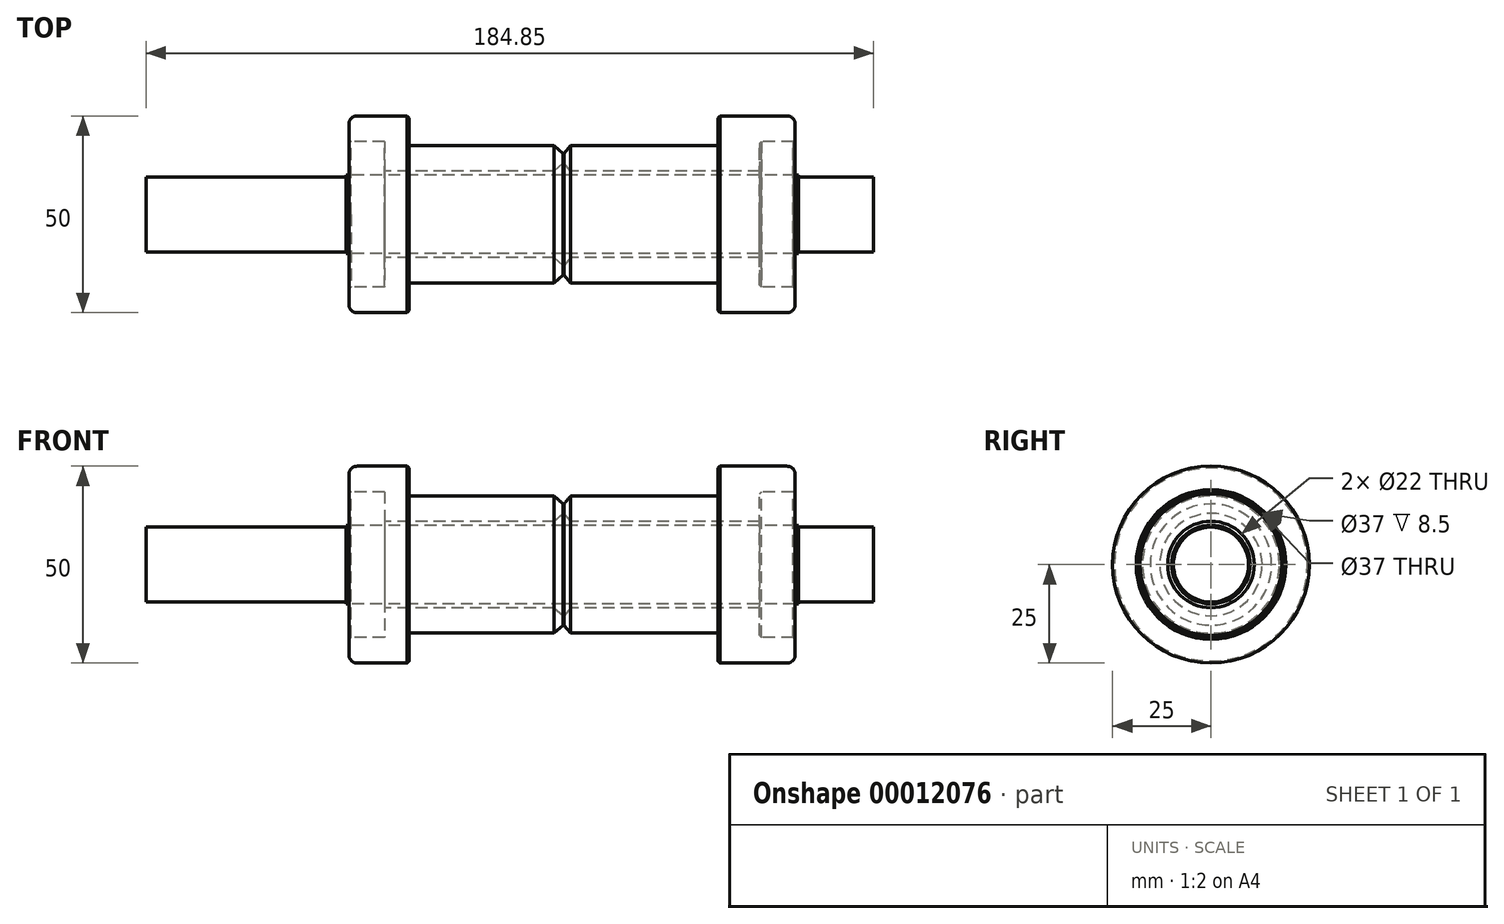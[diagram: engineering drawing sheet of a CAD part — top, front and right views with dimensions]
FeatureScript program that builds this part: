
annotation { "Feature Type Name" : "Feature", "Feature Type Description" : "" }
export const myFeature = defineFeature(function(context is Context, id is Id, definition is map)
    precondition{}
    {
        {
            var Q0;
            Q0=qCreatedBy(makeId("Front.planeOp"),FACE);
            var sketch = newSketch(context, id + "F0", { "sketchPlane" : qUnion([Q0])});
            skLineSegment(sketch, "E0", {"start": v(2, 25) * mm, "end": v(15.3, 25) * mm});
            skLineSegment(sketch, "E1", {"start": v(15.3, 25) * mm, "end": v(15.3, 17.4) * mm});
            skLineSegment(sketch, "E2", {"start": v(15.3, 17.4) * mm, "end": v(52.1, 17.4) * mm});
            skLineSegment(sketch, "E3", {"start": v(44.13, 11) * mm, "end": v(9, 11) * mm});
            skLineSegment(sketch, "E4", {"start": v(0, 23) * mm, "end": v(0, 18.5) * mm});
            skLineSegment(sketch, "E5.0", {"start": v(9, 18.5) * mm, "end": v(9, 11) * mm});
            skLineSegment(sketch, "E6", {"start": v(0, 18.5) * mm, "end": v(9, 18.5) * mm});
            skPoint(sketch, "E7.orphan", {"position": v(0, 11) * mm});
            skLineSegment(sketch, "E8", {"start": v(0, 0) * mm, "end": v(27.15, 0) * mm, "construction": true});
            skLineSegment(sketch, "E9", {"start": v(54.5, 56.17) * mm, "end": v(54.5, 17.4) * mm, "construction": true});
            skLineSegment(sketch, "E10.MirrorCS", {"start": v(113.3, 18.5) * mm, "end": v(104.3, 18.5) * mm});
            skLineSegment(sketch, "E11.MirrorCS", {"start": v(44.18, 11) * mm, "end": v(52.1, 11) * mm});
            skLineSegment(sketch, "E12.MirrorCS", {"start": v(111.3, 25) * mm, "end": v(93.7, 25) * mm});
            skLineSegment(sketch, "E13.MirrorCS", {"start": v(93.7, 25) * mm, "end": v(93.7, 17.4) * mm});
            skLineSegment(sketch, "E14.MirrorCS", {"start": v(93.7, 17.4) * mm, "end": v(61.18, 17.4) * mm});
            skPoint(sketch, "E15.MirrorP", {"position": v(109, 11) * mm});
            skPoint(sketch, "E16.orphan", {"position": v(109, 18.5) * mm});
            skLineSegment(sketch, "E17", {"start": v(104.3, 18.5) * mm, "end": v(104.3, 11) * mm});
            skPoint(sketch, "E18.MirrorCS.end.orphan", {"position": v(100, 11) * mm});
            skPoint(sketch, "E18.MirrorCS.start.orphan", {"position": v(100, 18.5) * mm});
            skLineSegment(sketch, "E19", {"start": v(-0.8, 10) * mm, "end": v(114.2, 10) * mm});
            skLineSegment(sketch, "E20", {"start": v(-51.6, 9.52) * mm, "end": v(-0.8, 9.52) * mm});
            skLineSegment(sketch, "E21", {"start": v(133.25, 9.53) * mm, "end": v(133.25, 0) * mm});
            skLineSegment(sketch, "E22", {"start": v(-51.6, 9.52) * mm, "end": v(-51.6, 0) * mm});
            skLineSegment(sketch, "E23", {"start": v(133.25, 0) * mm, "end": v(-51.6, 0) * mm});
            skPoint(sketch, "E23.startSnap0", {"position": v(133.25, 1.56) * mm});
            skLineSegment(sketch, "E24.trimOffspring", {"start": v(114.2, 9.53) * mm, "end": v(133.25, 9.53) * mm});
            skPoint(sketch, "E25.orphan", {"position": v(-51.6, 10) * mm});
            skLineSegment(sketch, "E26.trimOffspring", {"start": v(114.2, 10) * mm, "end": v(114.2, 9.53) * mm});
            skPoint(sketch, "E27.orphan", {"position": v(133.25, 10) * mm});
            skPoint(sketch, "E28.orphan", {"position": v(133.25, -6.87) * mm});
            skLineSegment(sketch, "E29", {"start": v(113.3, 23) * mm, "end": v(113.3, 18.5) * mm});
            skLineSegment(sketch, "E30", {"start": v(44.13, 11) * mm, "end": v(44.18, 11) * mm});
            skLineSegment(sketch, "E31.0", {"start": v(54.4, 15.4) * mm, "end": v(54.4, 13) * mm});
            skLineSegment(sketch, "E32.0", {"start": v(54.6, 15.4) * mm, "end": v(54.6, 13) * mm});
            skLineSegment(sketch, "E33.trimOffspring", {"start": v(54.5, 11) * mm, "end": v(54.5, -20.93) * mm, "construction": true});
            skLineSegment(sketch, "E34.trimOffspring", {"start": v(54.4, 0) * mm, "end": v(54.4, -20.93) * mm});
            skLineSegment(sketch, "E35", {"start": v(59.13, 17.4) * mm, "end": v(61.18, 17.4) * mm});
            skLineSegment(sketch, "E36.trimOffspring", {"start": v(56.3, 17.4) * mm, "end": v(59.13, 17.4) * mm});
            skPoint(sketch, "E37.visualSharp", {"position": v(54.6, 17.4) * mm});
            skPoint(sketch, "E38.visualSharp", {"position": v(54.4, 17.4) * mm});
            skLineSegment(sketch, "E39", {"start": v(54.6, 15.4) * mm, "end": v(56.3, 17.4) * mm});
            skLineSegment(sketch, "E40", {"start": v(52.1, 17.4) * mm, "end": v(54.4, 15.4) * mm});
            skLineSegment(sketch, "E41.trimOffspring", {"start": v(56.3, 11) * mm, "end": v(104.3, 11) * mm});
            skPoint(sketch, "E42.visualSharp", {"position": v(54.6, 11) * mm});
            skPoint(sketch, "E43.visualSharp", {"position": v(54.4, 11) * mm});
            skLineSegment(sketch, "E44", {"start": v(54.6, 13) * mm, "end": v(56.3, 11) * mm});
            skLineSegment(sketch, "E45", {"start": v(52.1, 11) * mm, "end": v(54.4, 13) * mm});
            skPoint(sketch, "E46.visualSharp", {"position": v(113.3, 25) * mm});
            skArc(sketch, "E46.filletArc", {"start": v(113.3, 23) * mm, "mid": v(112.71, 24.41) * mm, "end": v(111.3, 25) * mm});
            skPoint(sketch, "E47.visualSharp", {"position": v(0, 25) * mm});
            skArc(sketch, "E47.filletArc", {"start": v(2, 25) * mm, "mid": v(0.59, 24.41) * mm, "end": v(0, 23) * mm});
            skLineSegment(sketch, "E48", {"start": v(-0.8, 9.52) * mm, "end": v(-0.8, 10) * mm});
            skSolve(sketch);
        }
        {
            var Q0;
            Q0=makeQuery(id+"F0.imprint","IMPRINT",FACE,{"disambiguationData":[TD([[makeQuery(id+"F0.imprint","IMPRINT",EDGE,{"derivedFrom":sQuery(id+"F0.wireOp",EDGE,"E0")}),-1.0]])]});
            var Q1;
            Q1=makeQuery(id+"F0.imprint","IMPRINT",FACE,{"disambiguationData":[TD([[makeQuery(id+"F0.imprint","IMPRINT",EDGE,{"derivedFrom":sQuery(id+"F0.wireOp",EDGE,"E10.MirrorCS")}),-1.0]])]});
            var Q2;
            Q2=makeQuery(id+"F0.imprint","IMPRINT",FACE,{"disambiguationData":[TD([[makeQuery(id+"F0.imprint","IMPRINT",EDGE,{"derivedFrom":sQuery(id+"F0.wireOp",EDGE,"E19")}),-1.0]])]});
            var Q3;
            Q3=sQuery(id+"F0.wireOp",EDGE,"E8");
            var Q4;
            Q4=sQuery(id+"F0.wireOp",EDGE,"E8");
            revolve(context, id + "F1", {"entities" : qUnion([Q0, Q1, Q2]), "surfaceEntities" : qUnion([Q3]), "axis" : qUnion([Q4]), "revolveType" : RevolveType.FULL});
        }
        {
            var Q0;
            Q0=makeQuery(id+"F1.opRevolve","SWEPT_EDGE",EDGE,{"disambiguationData":[OSD([sQuery(id+"F0.wireOp",EDGE,"E0"),sQuery(id+"F0.wireOp",EDGE,"E1")])]});
            var Q1;
            Q1=makeQuery(id+"F1.opRevolve","SWEPT_EDGE",EDGE,{"disambiguationData":[OSD([sQuery(id+"F0.wireOp",EDGE,"E12.MirrorCS"),sQuery(id+"F0.wireOp",EDGE,"E13.MirrorCS")])]});
            var Q2;
            Q2=makeQuery(id+"F1.opRevolve","SWEPT_EDGE",EDGE,{"disambiguationData":[OSD([sQuery(id+"F0.wireOp",EDGE,"E10.MirrorCS"),sQuery(id+"F0.wireOp",EDGE,"KDt1QY0p-BJES-9n33-SlZV-N1xOpV1jrkDE")])]});
            var Q3;
            Q3=makeQuery(id+"F1.opRevolve","SWEPT_EDGE",EDGE,{"disambiguationData":[OSD([sQuery(id+"F0.wireOp",EDGE,"E4"),sQuery(id+"F0.wireOp",EDGE,"E6")])]});
            chamfer(context, id + "F2", {"entities" : qUnion([Q0, Q1, Q2, Q3]), "width" : .5 * mm, "tangentPropagation" : true});
        }
    });
